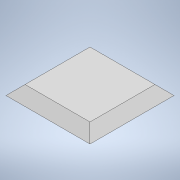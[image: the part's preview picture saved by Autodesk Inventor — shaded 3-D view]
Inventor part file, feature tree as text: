
AUTODESK INVENTOR PART (.ipt)
format: ipt  version: 2021 (Build 250183000, 183)  size: 96,256 bytes
history: native  units: in
note: dims shown in document units (in); Inventor stores cm internally (conversion verified against a paired STEP export)
features: extrude x1, chamfer x1, sketch x1
ambient origin geometry x8: Origin, YZ Plane, XZ Plane, XY Plane, X Axis, Y Axis, Z Axis, Center Point
bodies: Solid1 (feature_tree)
feature tree (3):
  extrude  "Extrusion1"  Depth=0.0591in
  chamfer  "Chamfer1"  Distance=0.0591in
  sketch  "Sketch1"  dims[d0=0.5197in d1=0.5197in d2=0.0591in d3=0.0in d4=0.0591in d5=0.0787in d6=45.0deg]
